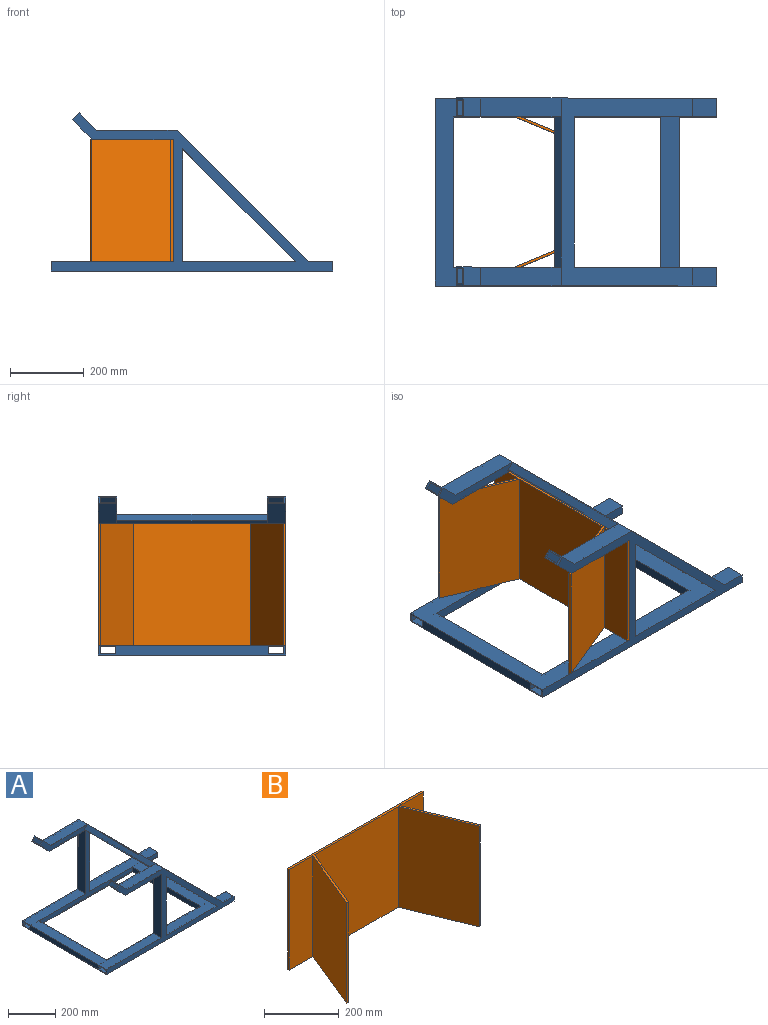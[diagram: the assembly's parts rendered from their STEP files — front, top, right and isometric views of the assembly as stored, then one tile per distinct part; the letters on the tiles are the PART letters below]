
ASSEMBLY  parts=2 mates=1
PART A: 83 faces, bbox 762x508x427.4 mm
  f0: plane 558.8x355.6mm, normal (0,-1,0), area 22258mm2, adj f6,f7,f9,f10,f11,f17,f32,f33
  f1: plane 403.32x345.08mm, normal (0,-1,0), area 13741.3mm2, adj f4,f7,f11,f12,f13,f34,f35
  f2: plane 283.23x71.84mm, normal (0,-1,0), area 7226.4mm2, adj f5,f7,f8,f14,f15,f16,f36
  f3: plane 508x25.4mm, normal (-1,0,0), area 11330.6mm2, adj f10,f11,f18,f23,f24,f31,f37,f38
  f4: plane 50.8x25.4mm, normal (1,0,0), area 504mm2, adj f1,f11,f12,f18,f24,f25,f31,f37
  f5: plane 50.8x17.96mm, normal (-0.71,0,0.71), area 504mm2, adj f2,f15,f16,f18,f28,f29,f31,f37
  f6: plane 304.8x50.8mm, normal (1,0,0), area 15483.8mm2, adj f0,f7,f17,f18
  f7: plane 508x337.64mm, normal (-0.71,0,-0.71), area 64440mm2, adj f0,f1,f2,f6,f17,f18,f35,f36
  f8: plane 218.83x50.8mm, normal (0,0,-1), area 11116.4mm2, adj f2,f9,f16,f18
  f9: plane 330.2x50.8mm, normal (-1,0,0), area 16774.2mm2, adj f0,f8,f10,f18
  f10: plane 508x330.2mm, normal (0,0,1), area 54193.4mm2, adj f0,f3,f9,f18,f32,f52,f57,f64
  f11: plane 762x508mm, normal (0,0,-1), area 118709.4mm2, adj f0,f1,f3,f4,f18,f32,f33,f34
  f12: plane 65.68x50.8mm, normal (0,0,1), area 3336.5mm2, adj f1,f4,f13,f18
  f13: plane 508x355.6mm, normal (0.71,0,0.71), area 71739.2mm2, adj f1,f12,f14,f18,f35,f36,f52,f55
  f14: plane 218.83x50.8mm, normal (0,0,1), area 11116.4mm2, adj f2,f13,f15,f18
  f15: plane 50.8x46.44mm, normal (0.71,0,0.71), area 3336.5mm2, adj f2,f5,f14,f18
  f16: plane 53.88x53.88mm, normal (-0.71,0,-0.71), area 3871mm2, adj f2,f5,f8,f18
  f17: plane 508x304.8mm, normal (0,0,1), area 51612.8mm2, adj f0,f6,f7,f18,f33,f34,f52,f59
  f18: plane 762x427.44mm, normal (0,1,0), area 47096.7mm2, adj f3,f4,f5,f6,f7,f8,f9,f10
  f19: plane 315.64x41.28mm, normal (-1,0,0), area 13028mm2, adj f20,f30,f31,f37
  f20: plane 315.64x315.64mm, normal (0.71,0,0.71), area 18424.4mm2, adj f19,f30,f31,f37
  f21: plane 220.69x41.28mm, normal (0,0,1), area 9108.8mm2, adj f22,f29,f31,f37
  f22: plane 336.55x41.28mm, normal (1,0,0), area 13891.1mm2, adj f21,f23,f31,f37
  f23: plane 333.38x41.28mm, normal (0,0,-1), area 13760.1mm2, adj f3,f22,f31,f37
  f24: plane 762x41.28mm, normal (0,0,1), area 31451.5mm2, adj f3,f4,f31,f37
  f25: plane 66.99x41.28mm, normal (0,0,-1), area 2765.2mm2, adj f4,f26,f31,f37
  f26: plane 355.6x355.6mm, normal (-0.71,0,-0.71), area 20757mm2, adj f25,f27,f31,f37
  f27: plane 218.83x41.28mm, normal (0,0,-1), area 9032.1mm2, adj f26,f28,f31,f37
  f28: plane 47.37x47.37mm, normal (-0.71,0,-0.71), area 2765.2mm2, adj f5,f27,f31,f37
  f29: plane 52.95x52.95mm, normal (0.71,0,0.71), area 3090.9mm2, adj f5,f21,f31,f37
  f30: plane 315.64x41.28mm, normal (0,0,-1), area 13028mm2, adj f19,f20,f31,f37
  f31: plane 762x422.02mm, normal (0,1,0), area 35552.3mm2, adj f3,f4,f5,f19,f20,f21,f22,f23
  f32: plane 406.4x25.4mm, normal (1,0,0), area 10322.6mm2, adj f0,f10,f11,f64
  f33: plane 406.4x25.4mm, normal (-1,0,0), area 10322.6mm2, adj f0,f11,f17,f64
  f34: plane 406.4x25.4mm, normal (1,0,0), area 10322.6mm2, adj f1,f11,f17,f63
  f35: plane 406.4x17.96mm, normal (0.71,0,-0.71), area 10322.6mm2, adj f1,f7,f13,f63
  f36: plane 406.4x17.96mm, normal (-0.71,0,0.71), area 10322.6mm2, adj f2,f7,f13,f62
  f37: plane 762x422.02mm, normal (0,-1,0), area 35552.3mm2, adj f3,f4,f5,f19,f20,f21,f22,f23
  f38: plane 762x422.02mm, normal (0,1,0), area 35552.3mm2, adj f3,f40,f41,f42,f43,f44,f45,f46
  f39: plane 762x422.02mm, normal (0,-1,0), area 35552.3mm2, adj f3,f40,f41,f42,f43,f44,f45,f46
  f40: plane 315.64x41.28mm, normal (0,0,-1), area 13028mm2, adj f38,f39,f50,f51
  f41: plane 52.95x52.95mm, normal (0.71,0,0.71), area 3090.9mm2, adj f38,f39,f49,f60
  f42: plane 47.37x47.37mm, normal (-0.71,0,-0.71), area 2765.2mm2, adj f38,f39,f43,f60
  f43: plane 218.83x41.28mm, normal (0,0,-1), area 9032.1mm2, adj f38,f39,f42,f44
  f44: plane 355.6x355.6mm, normal (-0.71,0,-0.71), area 20757mm2, adj f38,f39,f43,f45
  f45: plane 66.99x41.28mm, normal (0,0,-1), area 2765.2mm2, adj f38,f39,f44,f61
  f46: plane 762x41.28mm, normal (0,0,1), area 31451.6mm2, adj f3,f38,f39,f61
  f47: plane 333.38x41.28mm, normal (0,0,-1), area 13760.1mm2, adj f3,f38,f39,f48
  f48: plane 336.55x41.28mm, normal (1,0,0), area 13891.1mm2, adj f38,f39,f47,f49
  f49: plane 220.69x41.28mm, normal (0,0,1), area 9108.8mm2, adj f38,f39,f41,f48
  f50: plane 315.64x315.64mm, normal (0.71,0,0.71), area 18424.4mm2, adj f38,f39,f40,f51
  f51: plane 315.64x41.28mm, normal (-1,0,0), area 13028mm2, adj f38,f39,f40,f50
  f52: plane 762x427.44mm, normal (0,-1,0), area 47096.7mm2, adj f3,f7,f10,f11,f13,f17,f53,f54
  f53: plane 53.88x53.88mm, normal (-0.71,0,-0.71), area 3871mm2, adj f52,f58,f60,f62
  f54: plane 50.8x46.44mm, normal (0.71,0,0.71), area 3336.5mm2, adj f52,f55,f60,f62
  f55: plane 218.83x50.8mm, normal (0,0,1), area 11116.4mm2, adj f13,f52,f54,f62
  f56: plane 65.68x50.8mm, normal (0,0,1), area 3336.5mm2, adj f13,f52,f61,f63
  f57: plane 330.2x50.8mm, normal (-1,0,0), area 16774.2mm2, adj f10,f52,f58,f64
  f58: plane 218.83x50.8mm, normal (0,0,-1), area 11116.4mm2, adj f52,f53,f57,f62
  f59: plane 304.8x50.8mm, normal (1,0,0), area 15483.8mm2, adj f7,f17,f52,f64
  f60: plane 50.8x17.96mm, normal (-0.71,0,0.71), area 504mm2, adj f38,f39,f41,f42,f52,f53,f54,f62
  f61: plane 50.8x25.4mm, normal (1,0,0), area 504mm2, adj f11,f38,f39,f45,f46,f52,f56,f63
  f62: plane 283.23x71.84mm, normal (0,1,0), area 7226.4mm2, adj f7,f36,f53,f54,f55,f58,f60
  f63: plane 403.32x345.08mm, normal (0,1,0), area 13741.3mm2, adj f7,f11,f13,f34,f35,f56,f61
  f64: plane 558.8x355.6mm, normal (0,1,0), area 22258mm2, adj f7,f10,f11,f17,f32,f33,f57,f59
  f65: plane 44.9x44.9mm, normal (0,-1,0), area 846.8mm2, adj f66,f67,f68,f69
  f66: plane 406.4x31.43mm, normal (0.71,0,0.71), area 18064.5mm2, adj f65,f67,f69,f70
  f67: plane 406.4x13.47mm, normal (-0.71,0,0.71), area 7741.9mm2, adj f65,f66,f68,f70
  f68: plane 406.4x31.43mm, normal (-0.71,0,-0.71), area 18064.5mm2, adj f65,f67,f69,f70
  f69: plane 406.4x13.47mm, normal (0.71,0,-0.71), area 7741.9mm2, adj f65,f66,f68,f70
  f70: plane 44.9x44.9mm, normal (0,1,0), area 846.8mm2, adj f66,f67,f68,f69
  f71: plane 44.45x19.05mm, normal (0,-1,0), area 846.8mm2, adj f72,f73,f74,f75
  f72: plane 406.4x44.45mm, normal (0,0,1), area 18064.5mm2, adj f71,f73,f75,f76
  f73: plane 406.4x19.05mm, normal (-1,0,0), area 7741.9mm2, adj f71,f72,f74,f76
  f74: plane 406.4x44.45mm, normal (0,0,-1), area 18064.5mm2, adj f71,f73,f75,f76
  f75: plane 406.4x19.05mm, normal (1,0,0), area 7741.9mm2, adj f71,f72,f74,f76
  f76: plane 44.45x19.05mm, normal (0,1,0), area 846.8mm2, adj f72,f73,f74,f75
  f77: plane 44.45x19.05mm, normal (0,-1,0), area 846.8mm2, adj f78,f79,f80,f81
  f78: plane 406.4x44.45mm, normal (0,0,1), area 18064.5mm2, adj f77,f79,f81,f82
  f79: plane 406.4x19.05mm, normal (-1,0,0), area 7741.9mm2, adj f77,f78,f80,f82
  f80: plane 406.4x44.45mm, normal (0,0,-1), area 18064.5mm2, adj f77,f79,f81,f82
  f81: plane 406.4x19.05mm, normal (1,0,0), area 7741.9mm2, adj f77,f78,f80,f82
  f82: plane 44.45x19.05mm, normal (0,1,0), area 846.8mm2, adj f78,f79,f80,f81
PART B: 14 faces, bbox 508x224.7x330.2 mm
  f0: plane 330.2x88.9mm, normal (0,-1,0), area 29354.8mm2, adj f1,f11,f12,f13
  f1: plane 330.2x215.9mm, normal (-0.92,0.38,0), area 77097.3mm2, adj f0,f2,f12,f13
  f2: plane 330.2x5.87mm, normal (-0.38,-0.92,0), area 2096.8mm2, adj f1,f3,f12,f13
  f3: plane 330.2x218.32mm, normal (0.92,-0.38,0), area 77960.7mm2, adj f2,f4,f12,f13
  f4: plane 330.2x316.47mm, normal (0,-1,0), area 104496.9mm2, adj f3,f5,f12,f13
  f5: plane 330.2x218.32mm, normal (-0.92,-0.38,0), area 77960.7mm2, adj f4,f6,f12,f13
  f6: plane 330.2x5.87mm, normal (0.38,-0.92,0), area 2096.8mm2, adj f5,f7,f12,f13
  f7: plane 330.2x215.9mm, normal (0.92,0.38,0), area 77097.3mm2, adj f6,f8,f12,f13
  f8: plane 330.2x88.9mm, normal (0,-1,0), area 29354.8mm2, adj f7,f9,f12,f13
  f9: plane 330.2x6.35mm, normal (1,0,0), area 2096.8mm2, adj f8,f10,f12,f13
  f10: plane 508x330.2mm, normal (0,1,0), area 167741.6mm2, adj f9,f11,f12,f13
  f11: plane 330.2x6.35mm, normal (-1,0,0), area 2096.8mm2, adj f0,f10,f12,f13
  f12: plane 508x224.67mm, normal (0,0,1), area 6207.7mm2, adj f0,f1,f2,f3,f4,f5,f6,f7
  f13: plane 508x224.67mm, normal (0,0,-1), area 6207.7mm2, adj f0,f1,f2,f3,f4,f5,f6,f7
PLACE A rot(axis=(0,0,-1),0deg) t=(407.42,251.87,-96.62)mm fixed
PLACE B rot(axis=(0,0,-1),90deg) t=(-27.56,-2.13,-71.22)mm
MATE fastened A.f57 <-> B.f10  axis (-1,0,0) through (-24.38,-256.13,258.98)mm
